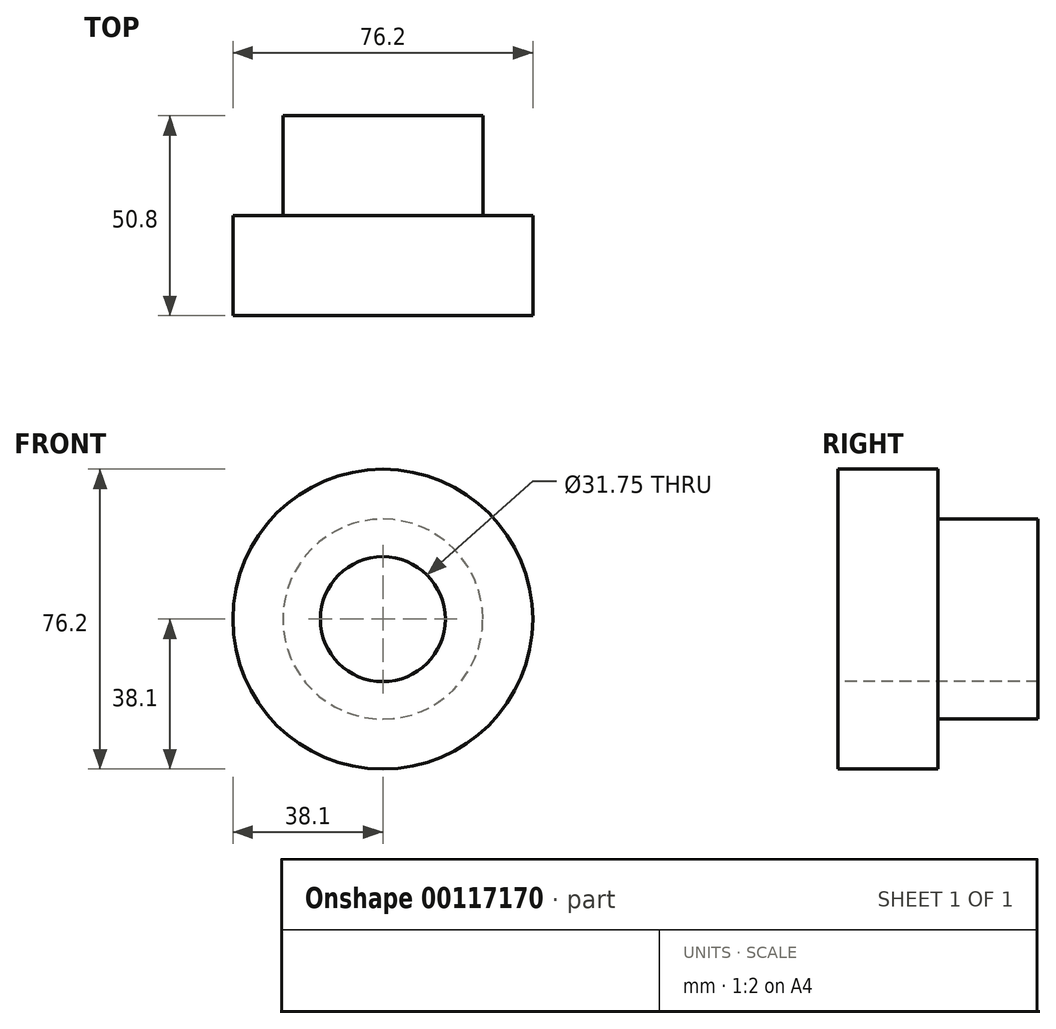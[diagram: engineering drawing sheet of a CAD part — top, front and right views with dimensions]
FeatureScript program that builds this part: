
annotation { "Feature Type Name" : "Feature", "Feature Type Description" : "" }
export const myFeature = defineFeature(function(context is Context, id is Id, definition is map)
    precondition{}
    {
        {
            var Q0;
            Q0=qCreatedBy(makeId("Front.planeOp"),FACE);
            var sketch = newSketch(context, id + "F0", { "sketchPlane" : qUnion([Q0])});
            skCircle(sketch, "E0", {"center": v(0, 0) * mm, "radius": 38.1 * mm});
            skSolve(sketch);
        }
        {
            var Q0;
            Q0=makeQuery(id+"F0.imprint","IMPRINT",FACE,{"disambiguationData":[TD([[makeQuery(id+"F0.imprint","IMPRINT",EDGE,{"derivedFrom":sQuery(id+"F0.wireOp",EDGE,"E0")}),1.0]])]});
            var sketch = newSketch(context, id + "F1", { "sketchPlane" : qUnion([Q0])});
            skCircle(sketch, "E1", {"center": v(0, 0) * mm, "radius": 38.2 * mm});
            skSolve(sketch);
        }
        {
            var Q0;
            Q0=makeQuery(id+"F0.imprint","IMPRINT",FACE,{"disambiguationData":[TD([[makeQuery(id+"F0.imprint","IMPRINT",EDGE,{"derivedFrom":sQuery(id+"F0.wireOp",EDGE,"E0")}),1.0]])]});
            var sketch = newSketch(context, id + "F2", { "sketchPlane" : qUnion([Q0])});
            skCircle(sketch, "E2", {"center": v(0, 0) * mm, "radius": 20.7 * mm});
            skSolve(sketch);
        }
        {
            var Q0;
            Q0=makeQuery(id+"F0.imprint","IMPRINT",FACE,{"disambiguationData":[TD([[makeQuery(id+"F0.imprint","IMPRINT",EDGE,{"derivedFrom":sQuery(id+"F0.wireOp",EDGE,"E0")}),1.0]])]});
            extrude(context, id + "F3", {"entities" : qUnion([Q0]), "depth" : 25.4 * mm});
        }
        {
            var Q0;
            Q0=qCreatedBy(makeId("Front.planeOp"),FACE);
            var sketch = newSketch(context, id + "F4", { "sketchPlane" : qUnion([Q0])});
            skCircle(sketch, "E3", {"center": v(0, 0) * mm, "radius": 20.51 * mm});
            skSolve(sketch);
        }
        {
            var Q0;
            Q0=qCreatedBy(makeId("Front.planeOp"),FACE);
            var sketch = newSketch(context, id + "F5", { "sketchPlane" : qUnion([Q0])});
            skCircle(sketch, "E4", {"center": v(0, 0) * mm, "radius": 25.4 * mm});
            skSolve(sketch);
        }
        {
            var Q0;
            Q0=makeQuery(id+"F5.imprint","IMPRINT",FACE,{"disambiguationData":[TD([[makeQuery(id+"F5.imprint","IMPRINT",EDGE,{"derivedFrom":sQuery(id+"F5.wireOp",EDGE,"E4")}),1.0]])]});
            extrude(context, id + "F6", {"entities" : qUnion([Q0]), "operationType" : NewBodyOperationType.ADD, "oppositeDirection" : true, "depth" : 25.4 * mm});
        }
        {
            var Q0;
            Q0=makeQuery(id+"F3.opExtrude","CAP_FACE",FACE,{"disambiguationData":[OSD([sQuery(id+"F0.wireOp",EDGE,"E0")])],"isStart":false});
            var sketch = newSketch(context, id + "F7", { "sketchPlane" : qUnion([Q0])});
            skCircle(sketch, "E5", {"center": v(0, 0) * mm, "radius": 8.2 * mm});
            skSolve(sketch);
        }
        {
            var Q0;
            Q0=sQuery(id+"F7.wireOp",VERTEX,"E5.center");
            var Q1;
            Q1=sQuery(id+"F4.wireOp",VERTEX,"E3.center");
            var Q2;
            Q2=sQuery(id+"F2.wireOp",VERTEX,"E2.center");
            var Q3;
            Q3=sQuery(id+"F1.wireOp",VERTEX,"E1.center");
            var Q4;
            Q4=makeQuery(id+"F3.opExtrude","SWEPT_BODY",BODY,{"disambiguationData":[OSD([sQuery(id+"F0.wireOp",EDGE,"E0")])]});
            hole(context, id + "F8", {"style" : HoleStyle.SIMPLE, "endStyle" : HoleEndStyle.THROUGH, "holeDiameter" : 31.75 * mm, "locations" : qUnion([Q0, Q1, Q2, Q3]), "scope" : qUnion([Q4]), "isTappedThrough" : true});
        }
    });
